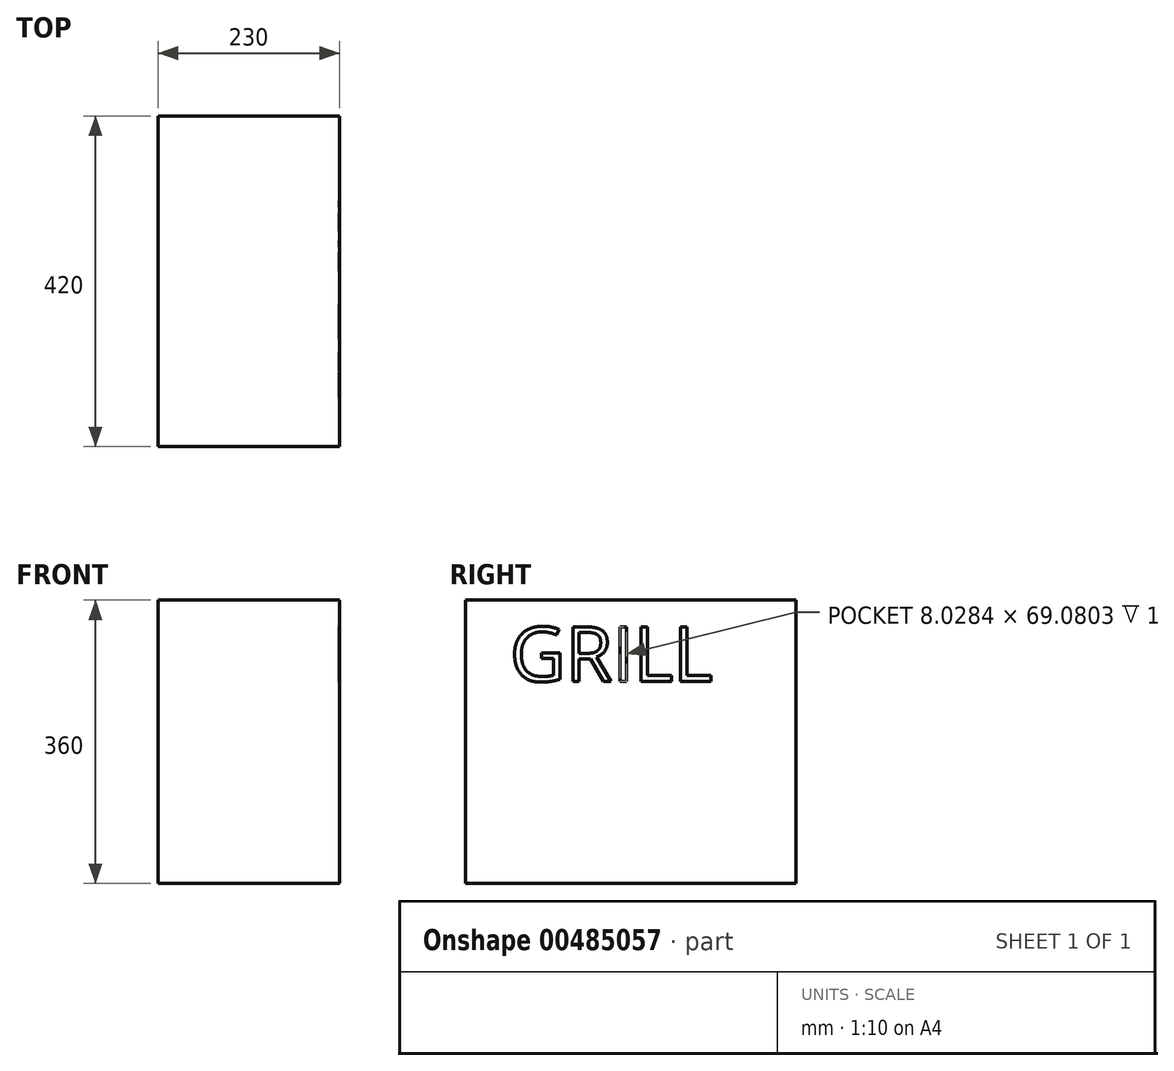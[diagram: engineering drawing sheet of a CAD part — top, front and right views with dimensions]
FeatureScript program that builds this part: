
annotation { "Feature Type Name" : "Feature", "Feature Type Description" : "" }
export const myFeature = defineFeature(function(context is Context, id is Id, definition is map)
    precondition{}
    {
        {
            var Q0;
            Q0=qCreatedBy(makeId("Top.planeOp"),FACE);
            var sketch = newSketch(context, id + "F0", { "sketchPlane" : qUnion([Q0])});
            skLineSegment(sketch, "E0.bottom", {"start": v(115, -210) * mm, "end": v(-115, -210) * mm});
            skLineSegment(sketch, "E0.top", {"start": v(115, 210) * mm, "end": v(-115, 210) * mm});
            skLineSegment(sketch, "E0.left", {"start": v(115, -210) * mm, "end": v(115, 210) * mm});
            skLineSegment(sketch, "E0.right", {"start": v(-115, -210) * mm, "end": v(-115, 210) * mm});
            skPoint(sketch, "E0.middle", {"position": v(0, 0) * mm});
            skSolve(sketch);
        }
        {
            var Q0;
            Q0 = qSketchRegion(id + "F0", true);
            extrude(context, id + "F1", {"entities" : qUnion([Q0]), "depth" : 360 * mm});
        }
        {
            var Q0;
            Q0=makeQuery(id+"F1.opExtrude","SWEPT_FACE",FACE,{"disambiguationData":[OSD([sQuery(id+"F0.wireOp",EDGE,"E0.left")])]});
            var sketch = newSketch(context, id + "F2", { "sketchPlane" : qUnion([Q0])});
            skText(sketch, "E1", { "text": "GRILL", "fontName": "OpenSans-Regular.ttf"});
            const initialGuessF2  = {"E1": [-0.1534, 0.2568, 1, 0, 0.06967]};
            skSetInitialGuess(sketch, initialGuessF2);
            skSolve(sketch);
        }
        {
            var Q0;
            Q0 = qSketchRegion(id + "F2", true);
            extrude(context, id + "F3", {"entities" : qUnion([Q0]), "operationType" : NewBodyOperationType.REMOVE, "oppositeDirection" : true, "depth" : 1 * mm});
        }
    });
